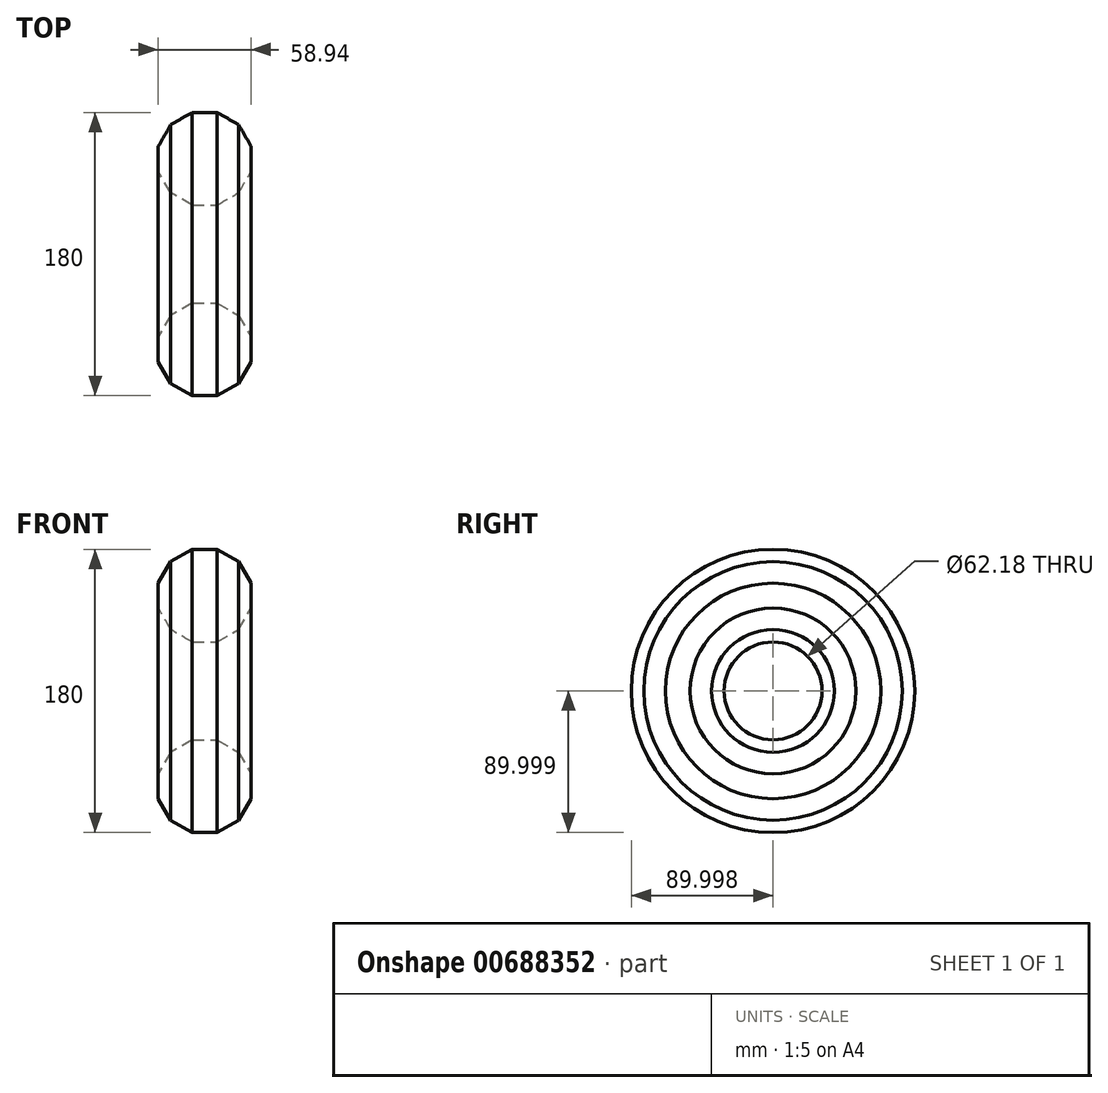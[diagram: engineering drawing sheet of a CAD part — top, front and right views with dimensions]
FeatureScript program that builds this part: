
annotation { "Feature Type Name" : "Feature", "Feature Type Description" : "" }
export const myFeature = defineFeature(function(context is Context, id is Id, definition is map)
    precondition{}
    {
        {
            var Q0;
            Q0=qCreatedBy(makeId("Top.planeOp"),FACE);
            var sketch = newSketch(context, id + "F0", { "sketchPlane" : qUnion([Q0])});
            skCircle(sketch, "E0.cCircle", {"center": v(0, 0) * mm, "radius": 29.47 * mm, "construction": true});
            skLineSegment(sketch, "E0.0", {"start": v(-29.47, -7.9) * mm, "end": v(-29.47, 7.9) * mm});
            skLineSegment(sketch, "E0.1", {"start": v(-29.47, 7.9) * mm, "end": v(-21.57, 21.57) * mm});
            skLineSegment(sketch, "E0.2", {"start": v(-21.57, 21.57) * mm, "end": v(-7.9, 29.47) * mm});
            skLineSegment(sketch, "E0.3", {"start": v(-7.9, 29.47) * mm, "end": v(7.9, 29.47) * mm});
            skLineSegment(sketch, "E0.4", {"start": v(7.9, 29.47) * mm, "end": v(21.57, 21.57) * mm});
            skLineSegment(sketch, "E0.5", {"start": v(21.57, 21.57) * mm, "end": v(29.47, 7.9) * mm});
            skLineSegment(sketch, "E0.6", {"start": v(29.47, 7.9) * mm, "end": v(29.47, -7.9) * mm});
            skLineSegment(sketch, "E0.7", {"start": v(29.47, -7.9) * mm, "end": v(21.57, -21.57) * mm});
            skLineSegment(sketch, "E0.8", {"start": v(21.57, -21.57) * mm, "end": v(7.9, -29.47) * mm});
            skLineSegment(sketch, "E0.9", {"start": v(7.9, -29.47) * mm, "end": v(-7.9, -29.47) * mm});
            skLineSegment(sketch, "E0.10", {"start": v(-7.9, -29.47) * mm, "end": v(-21.57, -21.57) * mm});
            skLineSegment(sketch, "E0.11", {"start": v(-21.57, -21.57) * mm, "end": v(-29.47, -7.9) * mm});
            skPoint(sketch, "E0.0.midPoint", {"position": v(-29.47, 0) * mm});
            skSolve(sketch);
        }
        {
            var Q0;
            Q0=qCreatedBy(makeId("Right.planeOp"),FACE);
            var sketch = newSketch(context, id + "F1", { "sketchPlane" : qUnion([Q0])});
            skCircle(sketch, "E1", {"center": v(60.52, 1.65) * mm, "radius": 60.54 * mm});
            skPoint(sketch, "E1.first.point", {"position": v(0, 0) * mm});
            skPoint(sketch, "E1.second.point", {"position": v(72.83, 60.92) * mm});
            skPoint(sketch, "E1.third.point", {"position": v(27.94, 52.68) * mm});
            skSolve(sketch);
        }
        {
            var Q0;
            Q0=makeQuery(id+"F0.imprint","IMPRINT",FACE,{"disambiguationData":[TD([[makeQuery(id+"F0.imprint","IMPRINT",EDGE,{"derivedFrom":sQuery(id+"F0.wireOp",EDGE,"E0.0")}),-1.0]])]});
            var Q1;
            Q1=sQuery(id+"F1.wireOp",EDGE,"E1");
            sweep(context, id + "F2", {"profiles" : qUnion([Q0]), "path" : qUnion([Q1])});
        }
    });
